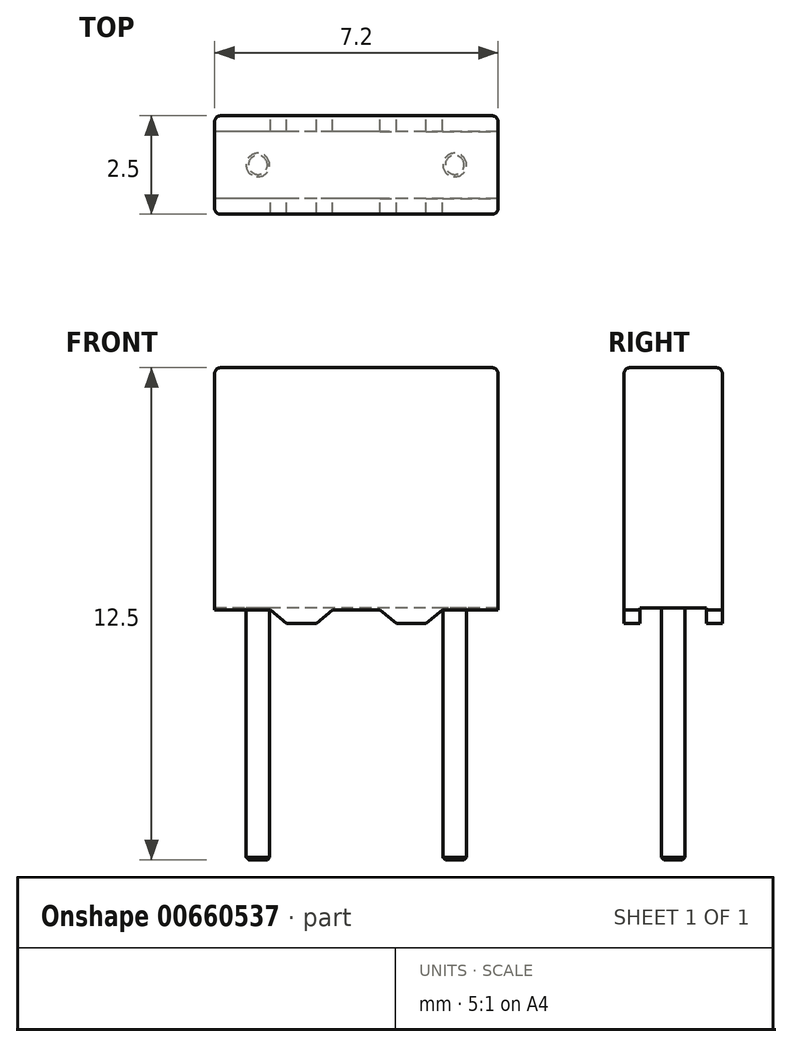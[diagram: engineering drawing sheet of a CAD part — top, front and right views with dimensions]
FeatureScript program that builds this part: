
annotation { "Feature Type Name" : "Feature", "Feature Type Description" : "" }
export const myFeature = defineFeature(function(context is Context, id is Id, definition is map)
    precondition{}
    {
        {
            var Q0;
            Q0=qCreatedBy(makeId("Top.planeOp"),FACE);
            var sketch = newSketch(context, id + "F0", { "sketchPlane" : qUnion([Q0])});
            skLineSegment(sketch, "E0.bottom", {"start": v(3.6, 1.25) * mm, "end": v(-3.6, 1.25) * mm});
            skLineSegment(sketch, "E0.top", {"start": v(3.6, -1.25) * mm, "end": v(-3.6, -1.25) * mm});
            skLineSegment(sketch, "E0.left", {"start": v(3.6, 1.25) * mm, "end": v(3.6, -1.25) * mm});
            skLineSegment(sketch, "E0.right", {"start": v(-3.6, 1.25) * mm, "end": v(-3.6, -1.25) * mm});
            skPoint(sketch, "E0.middle", {"position": v(0, 0) * mm});
            skSolve(sketch);
        }
        {
            var Q0;
            Q0=makeQuery(id+"F0.imprint","IMPRINT",FACE,{"disambiguationData":[TD([[makeQuery(id+"F0.imprint","IMPRINT",EDGE,{"derivedFrom":sQuery(id+"F0.wireOp",EDGE,"E0.bottom")}),1.0]])]});
            extrude(context, id + "F1", {"entities" : qUnion([Q0]), "depth" : 6.5 * mm, "offsetDistance" : 25 * mm});
        }
        {
            var Q0;
            Q0=makeQuery(id+"F1.opExtrude","CAP_FACE",FACE,{"disambiguationData":[OSD([sQuery(id+"F0.wireOp",EDGE,"E0.bottom"),sQuery(id+"F0.wireOp",EDGE,"E0.top"),sQuery(id+"F0.wireOp",EDGE,"E0.left"),sQuery(id+"F0.wireOp",EDGE,"E0.right")])],"isStart":true});
            var sketch = newSketch(context, id + "F2", { "sketchPlane" : qUnion([Q0])});
            skCircle(sketch, "E1", {"center": v(-2.5, 0) * mm, "radius": 0.3 * mm});
            skCircle(sketch, "E2", {"center": v(2.5, 0) * mm, "radius": 0.3 * mm});
            skSolve(sketch);
        }
        {
            var Q0;
            Q0=makeQuery(id+"F2.imprint","IMPRINT",FACE,{"disambiguationData":[TD([[makeQuery(id+"F2.imprint","IMPRINT",EDGE,{"derivedFrom":sQuery(id+"F2.wireOp",EDGE,"E1")}),1.0]])]});
            var Q1;
            Q1=makeQuery(id+"F2.imprint","IMPRINT",FACE,{"disambiguationData":[TD([[makeQuery(id+"F2.imprint","IMPRINT",EDGE,{"derivedFrom":sQuery(id+"F2.wireOp",EDGE,"E2")}),1.0]])]});
            extrude(context, id + "F3", {"entities" : qUnion([Q0, Q1]), "depth" : 6 * mm, "offsetDistance" : 25 * mm});
        }
        {
            var Q0;
            Q0=makeQuery(id+"F1.opExtrude","SWEPT_FACE",FACE,{"disambiguationData":[OSD([sQuery(id+"F0.wireOp",EDGE,"E0.right")])]});
            var sketch = newSketch(context, id + "F4", { "sketchPlane" : qUnion([Q0])});
            skLineSegment(sketch, "E3", {"start": v(-1.25, 0) * mm, "end": v(-0.85, 0) * mm});
            skLineSegment(sketch, "E4", {"start": v(-0.85, 0) * mm, "end": v(-0.85, 0.4) * mm});
            skLineSegment(sketch, "E5", {"start": v(-0.85, 0.4) * mm, "end": v(0, 0.4) * mm});
            skLineSegment(sketch, "E6.MirrorCS", {"start": v(0.85, 0.4) * mm, "end": v(0, 0.4) * mm});
            skLineSegment(sketch, "E7.MirrorCS", {"start": v(0.85, 0) * mm, "end": v(0.85, 0.4) * mm});
            skSolve(sketch);
        }
        {
            var Q0;
            {var subQ1=sQuery(id+"F4.wireOp",EDGE,"E4");Q0=makeQuery(id+"F4.imprint","IMPRINT",FACE,{"disambiguationData":[TD([[makeQuery(id+"F4.imprint","IMPRINT",EDGE,{"derivedFrom":subQ1}),-1.0]])]});}
            extrude(context, id + "F5", {"entities" : qUnion([Q0]), "operationType" : NewBodyOperationType.REMOVE, "oppositeDirection" : true, "depth" : 7.3 * mm, "offsetDistance" : 25 * mm});
        }
        {
            var Q0;
            Q0=makeQuery(id+"F1.opExtrude","SWEPT_FACE",FACE,{"disambiguationData":[OSD([sQuery(id+"F0.wireOp",EDGE,"E0.bottom")])]});
            var sketch = newSketch(context, id + "F6", { "sketchPlane" : qUnion([Q0])});
            skLineSegment(sketch, "E8", {"start": v(-3.6, 0.35) * mm, "end": v(-2.18, 0.35) * mm});
            skLineSegment(sketch, "E9", {"start": v(-2.18, 0.35) * mm, "end": v(-1.77, 0) * mm});
            skLineSegment(sketch, "E10", {"start": v(-1.77, 0) * mm, "end": v(-1.02, 0) * mm});
            skLineSegment(sketch, "E11", {"start": v(-1.02, 0) * mm, "end": v(-0.6, 0.35) * mm});
            skLineSegment(sketch, "E12", {"start": v(1.32, 0) * mm, "end": v(1.86, 0) * mm});
            skLineSegment(sketch, "E13", {"start": v(-0.6, 0.35) * mm, "end": v(0, 0.35) * mm});
            skLineSegment(sketch, "E14.MirrorCS", {"start": v(0.6, 0.35) * mm, "end": v(0, 0.35) * mm});
            skLineSegment(sketch, "E15.MirrorCS", {"start": v(1.02, 0) * mm, "end": v(0.6, 0.35) * mm});
            skLineSegment(sketch, "E16.MirrorCS", {"start": v(2.18, 0.35) * mm, "end": v(1.77, 0) * mm});
            skLineSegment(sketch, "E17.MirrorCS", {"start": v(3.6, 0.35) * mm, "end": v(2.18, 0.35) * mm});
            skSolve(sketch);
        }
        {
            var Q0;
            {var subQ0=sQuery(id+"F6.wireOp",EDGE,"E8");Q0=makeQuery(id+"F6.imprint","IMPRINT",FACE,{"disambiguationData":[TD([[makeQuery(id+"F6.imprint","IMPRINT",EDGE,{"derivedFrom":subQ0}),-1.0]])]});}
            var Q1;
            {var subQ0=sQuery(id+"F6.wireOp",EDGE,"E11");Q1=makeQuery(id+"F6.imprint","IMPRINT",FACE,{"disambiguationData":[TD([[makeQuery(id+"F6.imprint","IMPRINT",EDGE,{"derivedFrom":subQ0}),-1.0]])]});}
            var Q2;
            {var subQ5=sQuery(id+"F6.wireOp",EDGE,"E16.MirrorCS");Q2=makeQuery(id+"F6.imprint","IMPRINT",FACE,{"disambiguationData":[TD([[makeQuery(id+"F6.imprint","IMPRINT",EDGE,{"derivedFrom":subQ5}),1.0]])]});}
            extrude(context, id + "F7", {"entities" : qUnion([Q0, Q1, Q2]), "operationType" : NewBodyOperationType.REMOVE, "oppositeDirection" : true, "depth" : 6.5 * mm, "offsetDistance" : 25 * mm});
        }
        {
            var Q0;
            Q0=makeQuery(id+"F3.opExtrude","CAP_FACE",FACE,{"disambiguationData":[OSD([sQuery(id+"F2.wireOp",EDGE,"E1")])],"isStart":true});
            extrude(context, id + "F8", {"entities" : qUnion([Q0]), "operationType" : NewBodyOperationType.ADD, "depth" : 0.8 * mm, "offsetDistance" : 25 * mm});
        }
        {
            var Q0;
            Q0=makeQuery(id+"F3.opExtrude","CAP_FACE",FACE,{"disambiguationData":[OSD([sQuery(id+"F2.wireOp",EDGE,"E2")])],"isStart":true});
            extrude(context, id + "F9", {"entities" : qUnion([Q0]), "operationType" : NewBodyOperationType.ADD, "depth" : 0.8 * mm, "offsetDistance" : 25 * mm});
        }
        {
            var Q0;
            Q0=makeQuery(id+"F1.opExtrude","CAP_EDGE",EDGE,{"disambiguationData":[OSD([sQuery(id+"F0.wireOp",EDGE,"E0.bottom")])],"isStart":false});
            var Q1;
            Q1=makeQuery(id+"F1.opExtrude","SWEPT_EDGE",EDGE,{"disambiguationData":[OSD([sQuery(id+"F0.wireOp",EDGE,"E0.bottom"),sQuery(id+"F0.wireOp",EDGE,"E0.left")])]});
            var Q2;
            Q2=makeQuery(id+"F1.opExtrude","CAP_EDGE",EDGE,{"disambiguationData":[OSD([sQuery(id+"F0.wireOp",EDGE,"E0.left")])],"isStart":false});
            var Q3;
            Q3=makeQuery(id+"F1.opExtrude","CAP_EDGE",EDGE,{"disambiguationData":[OSD([sQuery(id+"F0.wireOp",EDGE,"E0.top")])],"isStart":false});
            var Q4;
            Q4=makeQuery(id+"F1.opExtrude","CAP_EDGE",EDGE,{"disambiguationData":[OSD([sQuery(id+"F0.wireOp",EDGE,"E0.right")])],"isStart":false});
            var Q5;
            Q5=makeQuery(id+"F1.opExtrude","SWEPT_EDGE",EDGE,{"disambiguationData":[OSD([sQuery(id+"F0.wireOp",EDGE,"E0.bottom"),sQuery(id+"F0.wireOp",EDGE,"E0.right")])]});
            var Q6;
            Q6=makeQuery(id+"F1.opExtrude","SWEPT_EDGE",EDGE,{"disambiguationData":[OSD([sQuery(id+"F0.wireOp",EDGE,"E0.top"),sQuery(id+"F0.wireOp",EDGE,"E0.left")])]});
            var Q7;
            Q7=makeQuery(id+"F1.opExtrude","SWEPT_EDGE",EDGE,{"disambiguationData":[OSD([sQuery(id+"F0.wireOp",EDGE,"E0.top"),sQuery(id+"F0.wireOp",EDGE,"E0.right")])]});
            fillet(context, id + "F10", {"entities" : qUnion([Q0, Q1, Q2, Q3, Q4, Q5, Q6, Q7]), "radius" : 0.15 * mm, "tangentPropagation" : true, "allowEdgeOverflow" : false});
        }
        {
            var Q0;
            Q0=makeQuery(id+"F3.opExtrude","CAP_EDGE",EDGE,{"disambiguationData":[OSD([sQuery(id+"F2.wireOp",EDGE,"E2")])],"isStart":false});
            var Q1;
            Q1=makeQuery(id+"F3.opExtrude","CAP_EDGE",EDGE,{"disambiguationData":[OSD([sQuery(id+"F2.wireOp",EDGE,"E1")])],"isStart":false});
            chamfer(context, id + "F11", {"entities" : qUnion([Q0, Q1]), "width" : 0.06 * mm, "tangentPropagation" : true});
        }
    });
